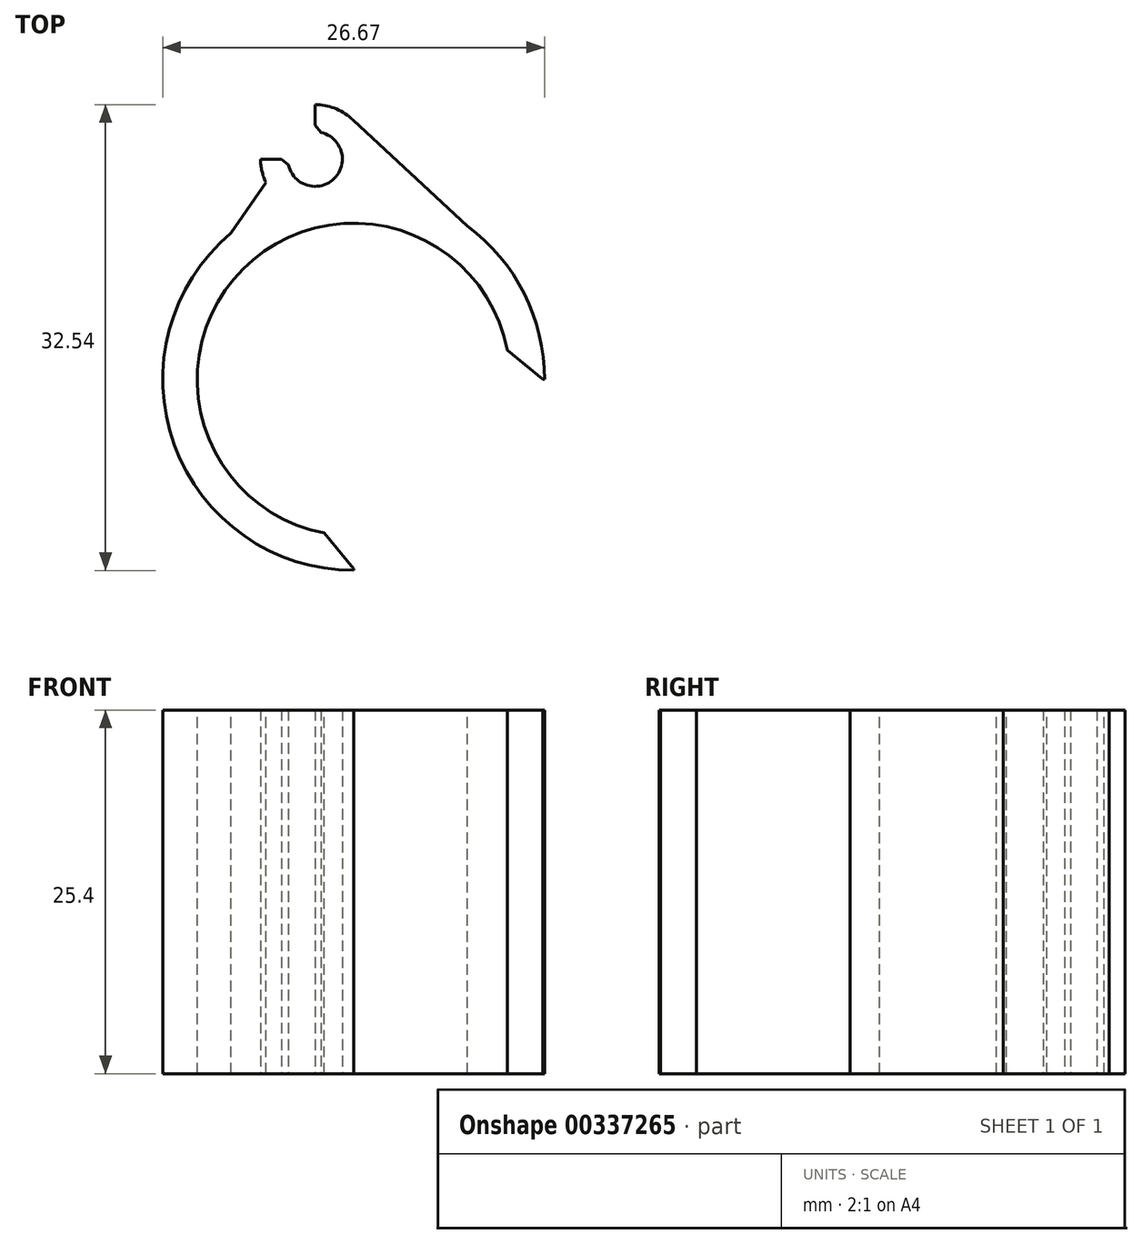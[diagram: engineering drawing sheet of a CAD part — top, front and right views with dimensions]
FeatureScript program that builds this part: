
annotation { "Feature Type Name" : "Feature", "Feature Type Description" : "" }
export const myFeature = defineFeature(function(context is Context, id is Id, definition is map)
    precondition{}
    {
        {
            var Q0;
            Q0=qCreatedBy(makeId("Top.planeOp"),FACE);
            var sketch = newSketch(context, id + "F0", { "sketchPlane" : qUnion([Q0])});
            skArc(sketch, "E0", {"start": v(-1.9, 0) * mm, "mid": v(1.35, -1.35) * mm, "end": v(0, 1.9) * mm});
            skArc(sketch, "E1", {"start": v(-3.81, 0) * mm, "mid": v(2.7, -2.7) * mm, "end": v(0, 3.81) * mm});
            skLineSegment(sketch, "E2", {"start": v(0, 1.9) * mm, "end": v(0, 3.81) * mm});
            skLineSegment(sketch, "E3", {"start": v(-1.9, 0) * mm, "end": v(-3.81, 0) * mm});
            skSolve(sketch);
        }
        {
            var Q0;
            Q0 = qSketchRegion(id + "F0", true);
            extrude(context, id + "F1", {"entities" : qUnion([Q0]), "depth" : 25.4 * mm});
        }
        {
            var Q0;
            Q0=makeQuery(id+"F1.opExtrude","CAP_FACE",FACE,{"disambiguationData":[OSD([sQuery(id+"F0.wireOp",EDGE,"E0"),sQuery(id+"F0.wireOp",EDGE,"E1"),sQuery(id+"F0.wireOp",EDGE,"E2"),sQuery(id+"F0.wireOp",EDGE,"E3")])],"isStart":false});
            var sketch = newSketch(context, id + "F2", { "sketchPlane" : qUnion([Q0])});
            skLineSegment(sketch, "E4", {"start": v(2.7, -2.7) * mm, "end": v(2.7, -15.4) * mm});
            skArc(sketch, "E5", {"start": v(13.62, -15.4) * mm, "mid": v(-5.03, -7.67) * mm, "end": v(2.7, -26.32) * mm});
            skArc(sketch, "E6", {"start": v(16.03, -15.4) * mm, "mid": v(12.3, -6.15) * mm, "end": v(3.2, -2.07) * mm});
            skLineSegment(sketch, "E7", {"start": v(2.52, 2.86) * mm, "end": v(10.63, -4.68) * mm});
            skPoint(sketch, "E7.startSnap0", {"position": v(0, 2.86) * mm});
            skLineSegment(sketch, "E8", {"start": v(-3.44, -1.64) * mm, "end": v(-5.86, -5.17) * mm});
            skLineSegment(sketch, "E9", {"start": v(13.62, -15.4) * mm, "end": v(16.03, -15.4) * mm});
            skLineSegment(sketch, "E10", {"start": v(2.7, -26.32) * mm, "end": v(2.7, -28.73) * mm});
            skArc(sketch, "E11.trimOffspring", {"start": v(2.66, 2.72) * mm, "mid": v(2.6, 2.8) * mm, "end": v(2.52, 2.86) * mm});
            skArc(sketch, "E12.trimOffspring", {"start": v(2.7, -2.7) * mm, "mid": v(2.96, -2.4) * mm, "end": v(3.2, -2.07) * mm});
            skArc(sketch, "E13", {"start": v(-3.44, -1.64) * mm, "mid": v(2.3, -3.04) * mm, "end": v(2.52, 2.86) * mm});
            skArc(sketch, "E14.trimOffspring", {"start": v(-2.3, -3.03) * mm, "mid": v(-10.4, -17.94) * mm, "end": v(2.7, -28.73) * mm});
            skSolve(sketch);
        }
        {
            var Q0;
            Q0 = qSketchRegion(id + "F2", true);
            extrude(context, id + "F3", {"entities" : qUnion([Q0]), "operationType" : NewBodyOperationType.ADD, "oppositeDirection" : true, "depth" : 25.4 * mm});
        }
        {
            var Q0;
            Q0=makeQuery(id+"F3.opExtrude","SWEPT_EDGE",EDGE,{"disambiguationData":[OSD([sQuery(id+"F2.wireOp",EDGE,"E5"),sQuery(id+"F2.wireOp",EDGE,"E10")])]});
            var Q1;
            Q1=makeQuery(id+"F3.opExtrude","SWEPT_EDGE",EDGE,{"disambiguationData":[OSD([sQuery(id+"F2.wireOp",EDGE,"E5"),sQuery(id+"F2.wireOp",EDGE,"E9")])]});
            chamfer(context, id + "F4", {"entities" : qUnion([Q0, Q1]), "width" : 2.54 * mm, "tangentPropagation" : true});
        }
        {
            var Q0;
            Q0=makeQuery(id+"F1.opExtrude","SWEPT_EDGE",EDGE,{"disambiguationData":[OSD([sQuery(id+"F0.wireOp",EDGE,"E0"),sQuery(id+"F0.wireOp",EDGE,"E3")])]});
            var Q1;
            Q1=makeQuery(id+"F1.opExtrude","SWEPT_EDGE",EDGE,{"disambiguationData":[OSD([sQuery(id+"F0.wireOp",EDGE,"E0"),sQuery(id+"F0.wireOp",EDGE,"E2")])]});
            chamfer(context, id + "F5", {"entities" : qUnion([Q0, Q1]), "width" : 0.5 * mm, "tangentPropagation" : true});
        }
    });
